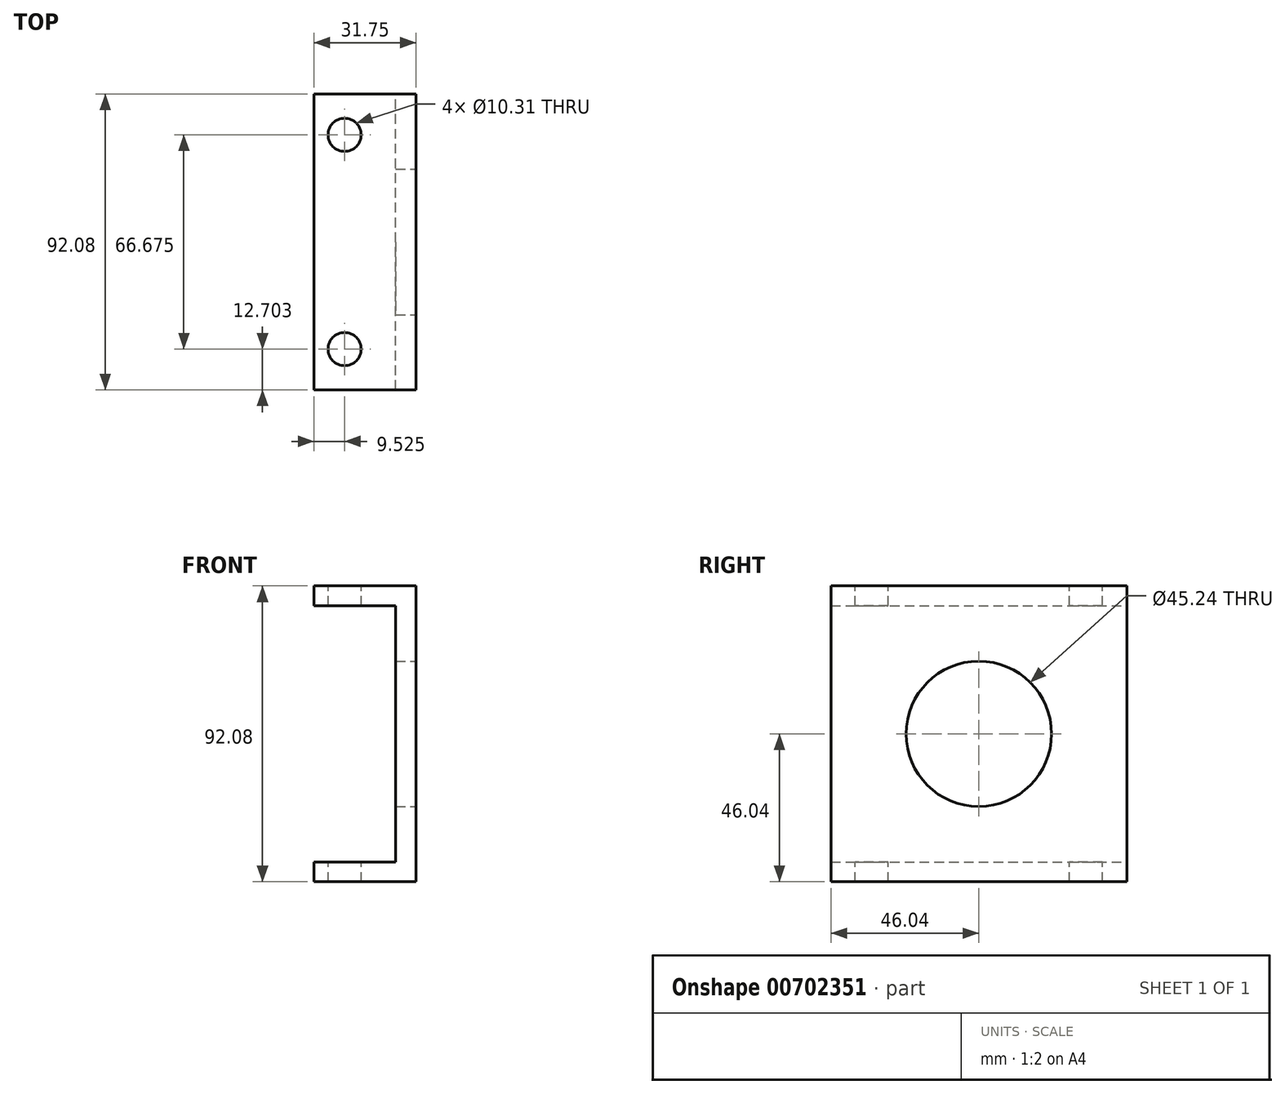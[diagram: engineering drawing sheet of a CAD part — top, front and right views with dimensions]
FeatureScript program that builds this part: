
annotation { "Feature Type Name" : "Feature", "Feature Type Description" : "" }
export const myFeature = defineFeature(function(context is Context, id is Id, definition is map)
    precondition{}
    {
        {
            var Q0;
            Q0=qCreatedBy(makeId("Right.planeOp"),FACE);
            var sketch = newSketch(context, id + "F0", { "sketchPlane" : qUnion([Q0])});
            skLineSegment(sketch, "E0.bottom", {"start": v(46.04, 46.04) * mm, "end": v(-46.04, 46.04) * mm});
            skLineSegment(sketch, "E0.top", {"start": v(46.04, -46.04) * mm, "end": v(-46.04, -46.04) * mm});
            skLineSegment(sketch, "E0.left", {"start": v(46.04, 46.04) * mm, "end": v(46.04, -46.04) * mm});
            skLineSegment(sketch, "E0.right", {"start": v(-46.04, 46.04) * mm, "end": v(-46.04, -46.04) * mm});
            skPoint(sketch, "E0.middle", {"position": v(0, 0) * mm});
            skSolve(sketch);
        }
        {
            var Q0;
            Q0 = qSketchRegion(id + "F0", true);
            extrude(context, id + "F1", {"entities" : qUnion([Q0]), "depth" : 25.4 * mm, "offsetDistance" : 25.4 * mm});
        }
        {
            var Q0;
            Q0=makeQuery(id+"F1.opExtrude","CAP_FACE",FACE,{"disambiguationData":[OSD([sQuery(id+"F0.wireOp",EDGE,"E0.bottom"),sQuery(id+"F0.wireOp",EDGE,"E0.top"),sQuery(id+"F0.wireOp",EDGE,"E0.left"),sQuery(id+"F0.wireOp",EDGE,"E0.right")])],"isStart":true});
            var sketch = newSketch(context, id + "F2", { "sketchPlane" : qUnion([Q0])});
            skLineSegment(sketch, "E1.bottom", {"start": v(82.55, 39.88) * mm, "end": v(-82.55, 39.88) * mm});
            skLineSegment(sketch, "E1.top", {"start": v(82.55, -39.88) * mm, "end": v(-82.55, -39.88) * mm});
            skLineSegment(sketch, "E1.left", {"start": v(82.55, 39.88) * mm, "end": v(82.55, -39.88) * mm});
            skLineSegment(sketch, "E1.right", {"start": v(-82.55, 39.88) * mm, "end": v(-82.55, -39.88) * mm});
            skPoint(sketch, "E1.middle", {"position": v(0, 0) * mm});
            skSolve(sketch);
        }
        {
            var Q0;
            Q0 = qSketchRegion(id + "F2", true);
            extrude(context, id + "F3", {"entities" : qUnion([Q0]), "operationType" : NewBodyOperationType.REMOVE, "oppositeDirection" : true, "depth" : 19.05 * mm, "offsetDistance" : 25.4 * mm});
        }
        {
            var Q0;
            Q0=makeQuery(id+"F1.opExtrude","CAP_FACE",FACE,{"disambiguationData":[OSD([sQuery(id+"F0.wireOp",EDGE,"E0.bottom"),sQuery(id+"F0.wireOp",EDGE,"E0.top"),sQuery(id+"F0.wireOp",EDGE,"E0.left"),sQuery(id+"F0.wireOp",EDGE,"E0.right")])],"isStart":false});
            var sketch = newSketch(context, id + "F4", { "sketchPlane" : qUnion([Q0])});
            skCircle(sketch, "E2", {"center": v(0, 0) * mm, "radius": 22.62 * mm});
            skSolve(sketch);
        }
        {
            var Q0;
            Q0 = qSketchRegion(id + "F4", true);
            extrude(context, id + "F5", {"entities" : qUnion([Q0]), "operationType" : NewBodyOperationType.REMOVE, "endBound" : BoundingType.THROUGH_ALL, "oppositeDirection" : true, "depth" : 25.4 * mm, "offsetDistance" : 25.4 * mm});
        }
        {
            var Q0;
            {var subQ0=sQuery(id+"F0.wireOp",EDGE,"E0.bottom");var subQ1=sQuery(id+"F0.wireOp",EDGE,"E0.right");var subQ2=sQuery(id+"F0.wireOp",EDGE,"E0.left");Q0=makeQuery(id+"F3.boolean.opBoolean","SPLIT",FACE,{"disambiguationData":[TD([makeQuery(id+"F1.opExtrude","SWEPT_FACE",FACE,{"disambiguationData":[OSD([subQ0])]})])],"derivedFrom":makeQuery(id+"F1.opExtrude","CAP_FACE",FACE,{"disambiguationData":[OSD([subQ0,sQuery(id+"F0.wireOp",EDGE,"E0.top"),subQ2,subQ1])],"isStart":true})});}
            var sketch = newSketch(context, id + "F6", { "sketchPlane" : qUnion([Q0])});
            skLineSegment(sketch, "E3.0", {"start": v(46.04, 39.88) * mm, "end": v(-46.04, 39.88) * mm});
            skLineSegment(sketch, "E3.1", {"start": v(46.04, 46.04) * mm, "end": v(46.04, 39.88) * mm});
            skLineSegment(sketch, "E3.2", {"start": v(-46.04, 46.04) * mm, "end": v(46.04, 46.04) * mm});
            skLineSegment(sketch, "E3.3", {"start": v(-46.04, 46.04) * mm, "end": v(-46.04, 39.88) * mm});
            skLineSegment(sketch, "E4.0", {"start": v(-46.04, -46.04) * mm, "end": v(46.04, -46.04) * mm});
            skLineSegment(sketch, "E4.1", {"start": v(46.04, -39.88) * mm, "end": v(-46.04, -39.88) * mm});
            skLineSegment(sketch, "E4.2", {"start": v(46.04, -39.88) * mm, "end": v(46.04, -46.04) * mm});
            skLineSegment(sketch, "E4.3", {"start": v(-46.04, -39.88) * mm, "end": v(-46.04, -46.04) * mm});
            skSolve(sketch);
        }
        {
            var Q0;
            Q0 = qSketchRegion(id + "F6", true);
            extrude(context, id + "F7", {"entities" : qUnion([Q0]), "operationType" : NewBodyOperationType.ADD, "depth" : 6.35 * mm, "offsetDistance" : 25.4 * mm});
        }
        {
            var Q0;
            Q0=makeQuery(id+"F7.boolean.opBoolean","MERGE",FACE,{"derivedFrom":[makeQuery(id+"F1.opExtrude","SWEPT_FACE",FACE,{"disambiguationData":[OSD([sQuery(id+"F0.wireOp",EDGE,"E0.bottom")])]}),makeQuery(id+"F7.opExtrude","SWEPT_FACE",FACE,{"disambiguationData":[OSD([sQuery(id+"F6.wireOp",EDGE,"E3.2")])]})]});
            var sketch = newSketch(context, id + "F8", { "sketchPlane" : qUnion([Q0])});
            skLineSegment(sketch, "E5", {"start": v(3.17, -46.04) * mm, "end": v(3.17, 46.04) * mm, "construction": true});
            skCircle(sketch, "E6", {"center": v(3.17, -33.34) * mm, "radius": 5.16 * mm});
            skCircle(sketch, "E7", {"center": v(3.17, 33.34) * mm, "radius": 5.16 * mm});
            skSolve(sketch);
        }
        {
            var Q0;
            Q0 = qSketchRegion(id + "F8", true);
            extrude(context, id + "F9", {"entities" : qUnion([Q0]), "operationType" : NewBodyOperationType.REMOVE, "endBound" : BoundingType.THROUGH_ALL, "oppositeDirection" : true, "depth" : 25.4 * mm, "offsetDistance" : 25.4 * mm});
        }
    });
